# Revit family: EDLQ-195-3000-xxx-SM
name_source: partatom
category: Leuchten
units: mm (PartAtom-declared; Revit-internal decimal feet)

## family parameters
Basisbauteil = Fläche
Beim Laden mit Abzugskörper schneiden = Nein
Bemaßung runder Anschluss = Durchmesser verwenden
Gemeinsam genutzt = Nein
Lichtquelle = Ja
OmniClass-Nummer = 23.80.70.11
OmniClass-Titel = Luminaries for Internal Lighting
Raumberechnungspunkt = Nein
Teiletyp = Normal

## types (5) — shared parameters
Baugruppenkennzeichen = D5020200
Datei für fotometrisches Netz = EDLQ 1953000-840 SM.IES
Emissionsform beim Rendern sichtbar = Nein
Farbfilter = 16777215
Farbtemperaturverschiebung bei Dämpfen der Lampe = <Keine Auswahl>
Hersteller = RIDI Leuchten GmbH
Lampe = LED
Neigungswinkel = 90.00°
Scheinlast = 23 VA
URL = www.ridi.de
Von Breite des Rechtecks ausssenden = 170 mm  [stored 0.557743 ft]
Von Länge des Rechtecks aussenden = 170 mm  [stored 0.557743 ft]
brand = RIDI
conformity mark = CE
electrical safety class = 1
height = 150 mm
ingress protection (IP) code = IP20
length = 195 mm  [stored 0.639764 ft]
nominal frequency = 50-60Hz
nominal voltage = 230
rated input power = 23
voltage type (AC, DC, UC) = AC
width = 195 mm  [stored 0.639764 ft]
zero-valued in all types: Vorgabe-Ansicht

## per-type parameters (varying)
| type | Modell | weight |
| EDLQ 195/3000-830 SM | 0321378 | 1,52 kg |
| EDLQ 195/3000-830 SM-DALI | 0331378 | 1,3 kg |
| EDLQ 195/3000-840 SM | 0321377 | 1,52 kg |
| EDLQ 195/3000-840 SM-DALI | 0331377 | 1,3 kg |
| EDLQ 195/3000-TW-SM | 0336730 | 1,44 kg |

note: column(s) folded — value = type name in every type: product name

note: [stored X ft] marks values corroborated as IEEE doubles in the binary element streams (Revit-internal decimal feet)
